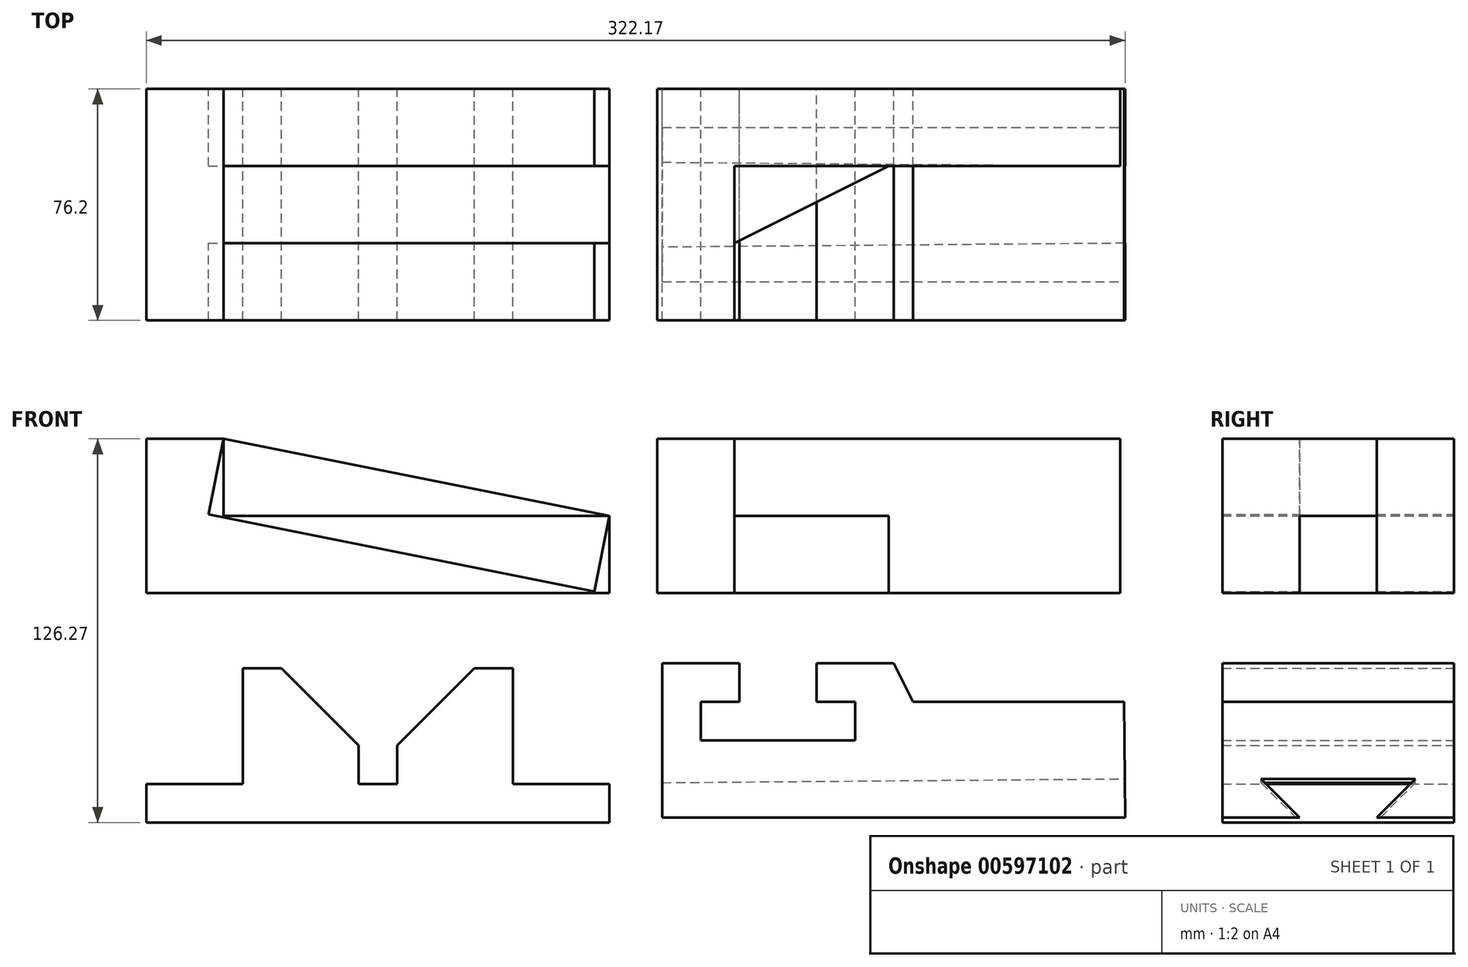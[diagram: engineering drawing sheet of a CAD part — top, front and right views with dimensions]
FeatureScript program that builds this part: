
annotation { "Feature Type Name" : "Feature", "Feature Type Description" : "" }
export const myFeature = defineFeature(function(context is Context, id is Id, definition is map)
    precondition{}
    {
        {
            var Q0;
            Q0=qCreatedBy(makeId("Front.planeOp"),FACE);
            var sketch = newSketch(context, id + "F0", { "sketchPlane" : qUnion([Q0])});
            skLineSegment(sketch, "E0", {"start": v(0, 0) * mm, "end": v(152.4, 0) * mm});
            skLineSegment(sketch, "E1", {"start": v(0, 0) * mm, "end": v(0, 50.8) * mm});
            skLineSegment(sketch, "E2", {"start": v(0, 50.8) * mm, "end": v(25.4, 50.8) * mm});
            skLineSegment(sketch, "E3", {"start": v(25.4, 50.8) * mm, "end": v(25.4, 25.4) * mm});
            skLineSegment(sketch, "E4", {"start": v(25.4, 25.4) * mm, "end": v(152.4, 25.4) * mm});
            skLineSegment(sketch, "E5", {"start": v(152.4, 25.4) * mm, "end": v(152.4, 0) * mm});
            skLineSegment(sketch, "E6", {"start": v(25.4, 50.8) * mm, "end": v(152.4, 25.4) * mm});
            skSolve(sketch);
        }
        {
            var Q0;
            Q0=makeQuery(id+"F0.imprint","IMPRINT",FACE,{"disambiguationData":[TD([[makeQuery(id+"F0.imprint","IMPRINT",EDGE,{"derivedFrom":sQuery(id+"F0.wireOp",EDGE,"E0")}),1.0]])]});
            extrude(context, id + "F1", {"entities" : qUnion([Q0]), "depth" : 76.2 * mm, "offsetDistance" : 25.4 * mm});
        }
        {
            var Q0;
            Q0=makeQuery(id+"F0.imprint","IMPRINT",FACE,{"disambiguationData":[TD([[makeQuery(id+"F0.imprint","IMPRINT",EDGE,{"derivedFrom":sQuery(id+"F0.wireOp",EDGE,"E3")}),1.0]])]});
            extrude(context, id + "F2", {"entities" : qUnion([Q0]), "depth" : 76.2 * mm, "offsetDistance" : 25.4 * mm});
        }
        {
            var Q0;
            Q0=makeQuery(id+"F2.opExtrude","SWEPT_FACE",FACE,{"disambiguationData":[OSD([sQuery(id+"F0.wireOp",EDGE,"E6")])]});
            var sketch = newSketch(context, id + "F3", { "sketchPlane" : qUnion([Q0])});
            skLineSegment(sketch, "E7", {"start": v(14.94, -50.8) * mm, "end": v(144.46, -50.8) * mm});
            skLineSegment(sketch, "E8", {"start": v(144.46, -50.8) * mm, "end": v(144.46, -76.2) * mm});
            skLineSegment(sketch, "E9", {"start": v(144.46, -76.2) * mm, "end": v(14.94, -76.2) * mm});
            skLineSegment(sketch, "E10", {"start": v(14.94, -76.2) * mm, "end": v(14.94, -50.8) * mm});
            skLineSegment(sketch, "E11", {"start": v(14.94, 0) * mm, "end": v(14.94, -25.4) * mm});
            skLineSegment(sketch, "E12", {"start": v(14.94, -25.4) * mm, "end": v(144.46, -25.4) * mm});
            skLineSegment(sketch, "E13", {"start": v(144.46, -25.4) * mm, "end": v(144.46, 0) * mm});
            skLineSegment(sketch, "E14", {"start": v(144.46, 0) * mm, "end": v(14.94, 0) * mm});
            skSolve(sketch);
        }
        {
            var Q0;
            Q0=makeQuery(id+"F3.imprint","IMPRINT",FACE,{"disambiguationData":[TD([[makeQuery(id+"F3.imprint","IMPRINT",EDGE,{"derivedFrom":sQuery(id+"F3.wireOp",EDGE,"E7")}),-1.0]])]});
            extrude(context, id + "F4", {"entities" : qUnion([Q0]), "operationType" : NewBodyOperationType.REMOVE, "oppositeDirection" : true, "depth" : 25.4 * mm, "offsetDistance" : 25.4 * mm});
        }
        {
            var Q0;
            Q0=makeQuery(id+"F3.imprint","IMPRINT",FACE,{"disambiguationData":[TD([[makeQuery(id+"F3.imprint","IMPRINT",EDGE,{"derivedFrom":sQuery(id+"F3.wireOp",EDGE,"E11")}),-1.0]])]});
            extrude(context, id + "F5", {"entities" : qUnion([Q0]), "operationType" : NewBodyOperationType.REMOVE, "oppositeDirection" : true, "depth" : 25.4 * mm, "offsetDistance" : 25.4 * mm});
        }
        {
            var Q0;
            Q0=qCreatedBy(makeId("Front.planeOp"),FACE);
            var sketch = newSketch(context, id + "F6", { "sketchPlane" : qUnion([Q0])});
            skLineSegment(sketch, "E15", {"start": v(320.54, 0) * mm, "end": v(320.54, 50.8) * mm});
            skLineSegment(sketch, "E16", {"start": v(320.54, 50.8) * mm, "end": v(168.14, 50.8) * mm});
            skLineSegment(sketch, "E17", {"start": v(168.14, 50.8) * mm, "end": v(168.14, 0) * mm});
            skLineSegment(sketch, "E18", {"start": v(168.14, 0) * mm, "end": v(320.54, 0) * mm});
            skLineSegment(sketch, "E19", {"start": v(168.14, 0) * mm, "end": v(193.54, 0) * mm});
            skLineSegment(sketch, "E20", {"start": v(193.54, 0) * mm, "end": v(193.54, 50.8) * mm});
            skLineSegment(sketch, "E21", {"start": v(193.54, 50.8) * mm, "end": v(168.14, 50.8) * mm});
            skSolve(sketch);
        }
        {
            var Q0;
            Q0=makeQuery(id+"F6.imprint","IMPRINT",FACE,{"disambiguationData":[TD([[makeQuery(id+"F6.imprint","IMPRINT",EDGE,{"derivedFrom":sQuery(id+"F6.wireOp",EDGE,"E15")}),1.0]])]});
            extrude(context, id + "F7", {"entities" : qUnion([Q0]), "depth" : 25.4 * mm, "offsetDistance" : 25.4 * mm});
        }
        {
            var Q0;
            Q0=makeQuery(id+"F6.imprint","IMPRINT",FACE,{"disambiguationData":[TD([[makeQuery(id+"F6.imprint","IMPRINT",EDGE,{"derivedFrom":sQuery(id+"F6.wireOp",EDGE,"E17")}),1.0]])]});
            extrude(context, id + "F8", {"entities" : qUnion([Q0]), "operationType" : NewBodyOperationType.ADD, "depth" : 76.2 * mm, "offsetDistance" : 25.4 * mm});
        }
        {
            var Q0;
            Q0=makeQuery(id+"F7.opExtrude","CAP_FACE",FACE,{"disambiguationData":[OSD([sQuery(id+"F6.wireOp",EDGE,"E15"),sQuery(id+"F6.wireOp",EDGE,"E16"),sQuery(id+"F6.wireOp",EDGE,"E18"),sQuery(id+"F6.wireOp",EDGE,"E20")])],"isStart":false});
            var sketch = newSketch(context, id + "F9", { "sketchPlane" : qUnion([Q0])});
            skLineSegment(sketch, "E22", {"start": v(193.54, 0) * mm, "end": v(193.54, 25.4) * mm});
            skLineSegment(sketch, "E23", {"start": v(193.54, 25.4) * mm, "end": v(244.34, 25.4) * mm});
            skLineSegment(sketch, "E24", {"start": v(244.34, 25.4) * mm, "end": v(244.34, 0) * mm});
            skLineSegment(sketch, "E25", {"start": v(244.34, 0) * mm, "end": v(193.54, 0) * mm});
            skSolve(sketch);
        }
        {
            var Q0;
            Q0=makeQuery(id+"F9.imprint","IMPRINT",FACE,{"disambiguationData":[TD([[makeQuery(id+"F9.imprint","IMPRINT",EDGE,{"derivedFrom":sQuery(id+"F9.wireOp",EDGE,"E22")}),-1.0]])]});
            extrude(context, id + "F10", {"entities" : qUnion([Q0]), "operationType" : NewBodyOperationType.ADD, "depth" : 25.4 * mm, "offsetDistance" : 25.4 * mm});
        }
        {
            var Q0;
            Q0=makeQuery(id+"F10.opExtrude","SWEPT_FACE",FACE,{"disambiguationData":[OSD([sQuery(id+"F9.wireOp",EDGE,"E23")])]});
            var sketch = newSketch(context, id + "F11", { "sketchPlane" : qUnion([Q0])});
            skLineSegment(sketch, "E26", {"start": v(193.54, -50.8) * mm, "end": v(244.34, -25.4) * mm});
            skLineSegment(sketch, "E27", {"start": v(244.34, -25.4) * mm, "end": v(244.34, -50.8) * mm});
            skLineSegment(sketch, "E28", {"start": v(244.34, -50.8) * mm, "end": v(193.54, -50.8) * mm});
            skSolve(sketch);
        }
        {
            var Q0;
            Q0=makeQuery(id+"F11.imprint","IMPRINT",FACE,{"disambiguationData":[TD([[makeQuery(id+"F11.imprint","IMPRINT",EDGE,{"derivedFrom":sQuery(id+"F11.wireOp",EDGE,"E26")}),-1.0]])]});
            extrude(context, id + "F12", {"entities" : qUnion([Q0]), "operationType" : NewBodyOperationType.REMOVE, "oppositeDirection" : true, "depth" : 25.4 * mm, "offsetDistance" : 25.4 * mm});
        }
        {
            var Q0;
            Q0=qCreatedBy(makeId("Front.planeOp"),FACE);
            var sketch = newSketch(context, id + "F13", { "sketchPlane" : qUnion([Q0])});
            skLineSegment(sketch, "E29", {"start": v(0, -75.47) * mm, "end": v(152.4, -75.47) * mm});
            skLineSegment(sketch, "E30", {"start": v(152.4, -75.47) * mm, "end": v(152.4, -62.77) * mm});
            skLineSegment(sketch, "E31", {"start": v(152.4, -62.77) * mm, "end": v(120.65, -62.77) * mm});
            skLineSegment(sketch, "E32", {"start": v(120.65, -62.77) * mm, "end": v(120.65, -24.67) * mm});
            skLineSegment(sketch, "E33", {"start": v(120.65, -24.67) * mm, "end": v(107.95, -24.67) * mm});
            skLineSegment(sketch, "E34", {"start": v(107.95, -24.67) * mm, "end": v(82.55, -50.07) * mm});
            skLineSegment(sketch, "E35", {"start": v(82.55, -50.07) * mm, "end": v(82.55, -62.77) * mm});
            skLineSegment(sketch, "E36", {"start": v(82.55, -62.77) * mm, "end": v(69.85, -62.77) * mm});
            skLineSegment(sketch, "E37", {"start": v(69.85, -62.77) * mm, "end": v(69.85, -50.07) * mm});
            skLineSegment(sketch, "E38", {"start": v(69.85, -50.07) * mm, "end": v(44.45, -24.67) * mm});
            skLineSegment(sketch, "E39", {"start": v(44.45, -24.67) * mm, "end": v(31.75, -24.67) * mm});
            skLineSegment(sketch, "E40", {"start": v(31.75, -24.67) * mm, "end": v(31.75, -62.77) * mm});
            skLineSegment(sketch, "E41", {"start": v(31.75, -62.77) * mm, "end": v(0, -62.77) * mm});
            skLineSegment(sketch, "E42", {"start": v(0, -62.77) * mm, "end": v(0, -75.47) * mm});
            skSolve(sketch);
        }
        {
            var Q0;
            Q0=qCreatedBy(makeId("Front.planeOp"),FACE);
            var sketch = newSketch(context, id + "F14", { "sketchPlane" : qUnion([Q0])});
            skLineSegment(sketch, "E43", {"start": v(169.77, -73.8) * mm, "end": v(322.17, -73.8) * mm});
            skLineSegment(sketch, "E44", {"start": v(169.77, -73.8) * mm, "end": v(169.77, -23) * mm});
            skLineSegment(sketch, "E45", {"start": v(169.77, -23) * mm, "end": v(195.17, -23) * mm});
            skLineSegment(sketch, "E46", {"start": v(195.17, -23) * mm, "end": v(195.17, -35.7) * mm});
            skLineSegment(sketch, "E47", {"start": v(195.17, -35.7) * mm, "end": v(182.47, -35.7) * mm});
            skLineSegment(sketch, "E48", {"start": v(182.47, -35.7) * mm, "end": v(182.47, -48.4) * mm});
            skLineSegment(sketch, "E49", {"start": v(182.47, -48.4) * mm, "end": v(233.27, -48.4) * mm});
            skLineSegment(sketch, "E50", {"start": v(233.27, -48.4) * mm, "end": v(233.27, -35.7) * mm});
            skLineSegment(sketch, "E51", {"start": v(233.27, -35.7) * mm, "end": v(220.57, -35.7) * mm});
            skLineSegment(sketch, "E52", {"start": v(220.57, -35.7) * mm, "end": v(220.57, -23) * mm});
            skLineSegment(sketch, "E53", {"start": v(220.57, -23) * mm, "end": v(245.97, -23) * mm});
            skLineSegment(sketch, "E54", {"start": v(245.97, -23) * mm, "end": v(252.32, -35.7) * mm});
            skLineSegment(sketch, "E55", {"start": v(252.32, -35.7) * mm, "end": v(321.85, -35.7) * mm});
            skLineSegment(sketch, "E56", {"start": v(322.17, -73.8) * mm, "end": v(321.85, -35.7) * mm});
            skSolve(sketch);
        }
        {
            var Q0;
            Q0=makeQuery(id+"F13.imprint","IMPRINT",FACE,{"disambiguationData":[TD([[makeQuery(id+"F13.imprint","IMPRINT",EDGE,{"derivedFrom":sQuery(id+"F13.wireOp",EDGE,"E29")}),1.0]])]});
            extrude(context, id + "F15", {"entities" : qUnion([Q0]), "depth" : 76.2 * mm, "offsetDistance" : 25.4 * mm});
        }
        {
            var Q0;
            Q0=makeQuery(id+"F14.imprint","IMPRINT",FACE,{"disambiguationData":[TD([[makeQuery(id+"F14.imprint","IMPRINT",EDGE,{"derivedFrom":sQuery(id+"F14.wireOp",EDGE,"E43")}),1.0]])]});
            extrude(context, id + "F16", {"entities" : qUnion([Q0]), "depth" : 76.2 * mm, "offsetDistance" : 25.4 * mm});
        }
        {
            var Q0;
            Q0=makeQuery(id+"F16.opExtrude","SWEPT_FACE",FACE,{"disambiguationData":[OSD([sQuery(id+"F14.wireOp",EDGE,"E56")])]});
            var sketch = newSketch(context, id + "F17", { "sketchPlane" : qUnion([Q0])});
            skLineSegment(sketch, "E57", {"start": v(-76.2, -76.5) * mm, "end": v(-50.8, -76.5) * mm});
            skLineSegment(sketch, "E58", {"start": v(-50.8, -76.5) * mm, "end": v(-63.5, -63.8) * mm});
            skLineSegment(sketch, "E59", {"start": v(-63.5, -63.8) * mm, "end": v(-12.7, -63.8) * mm});
            skLineSegment(sketch, "E60", {"start": v(-12.7, -63.8) * mm, "end": v(-25.4, -76.5) * mm});
            skLineSegment(sketch, "E61", {"start": v(-25.4, -76.5) * mm, "end": v(0, -76.5) * mm});
            skSolve(sketch);
        }
        {
            var Q0;
            {var subQ0=sQuery(id+"F17.wireOp",EDGE,"E58");Q0=makeQuery(id+"F17.imprint","IMPRINT",FACE,{"disambiguationData":[TD([[makeQuery(id+"F17.imprint","IMPRINT",EDGE,{"derivedFrom":subQ0}),-1.0]])]});}
            extrude(context, id + "F18", {"entities" : qUnion([Q0]), "operationType" : NewBodyOperationType.REMOVE, "oppositeDirection" : true, "depth" : 152.4 * mm, "offsetDistance" : 25.4 * mm});
        }
    });
